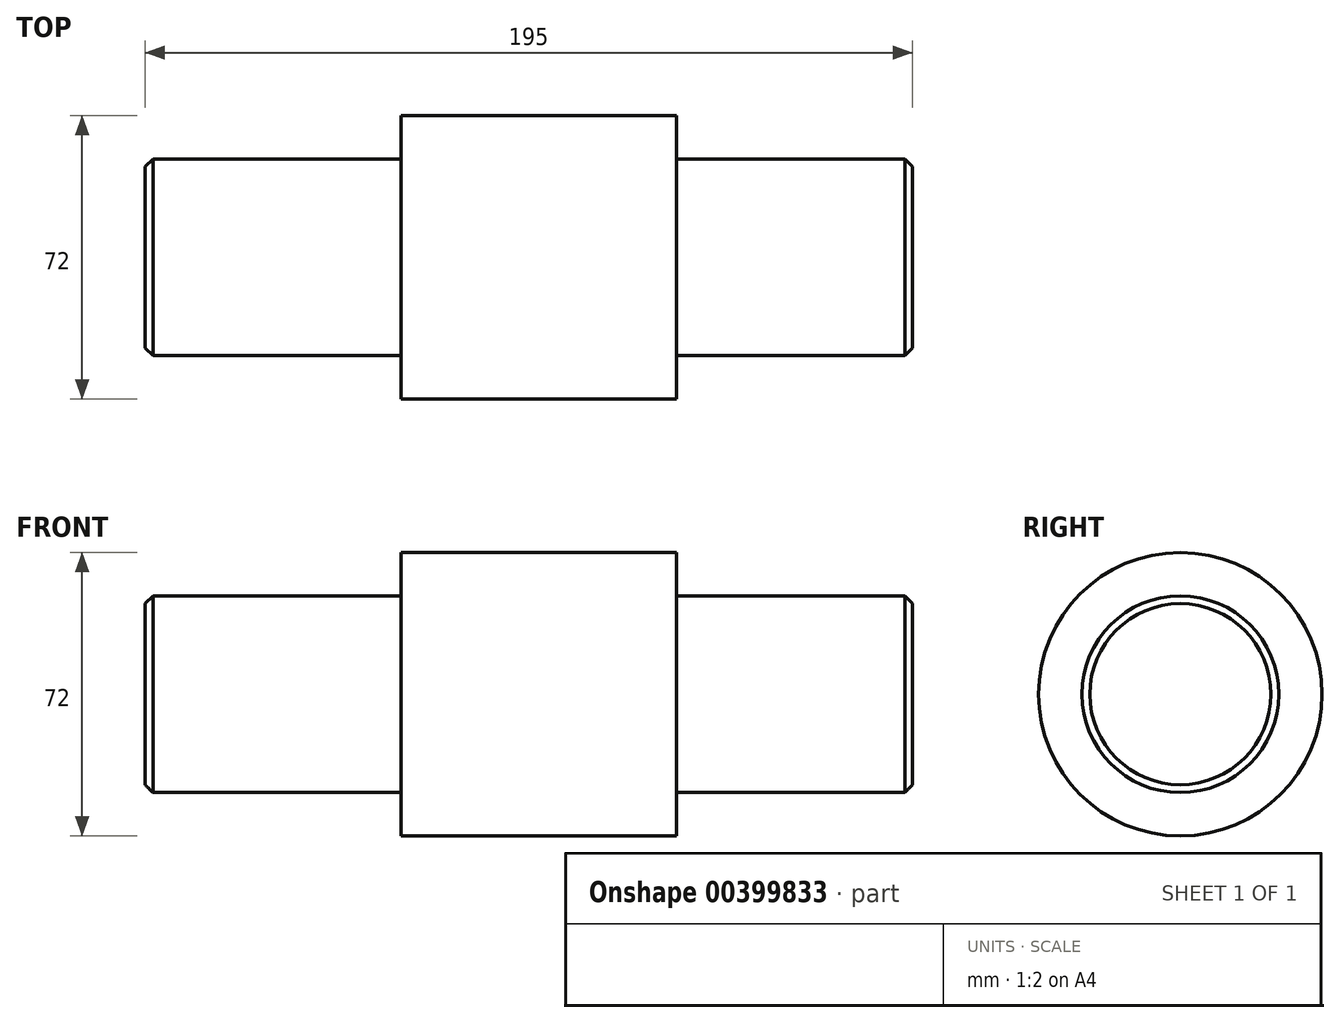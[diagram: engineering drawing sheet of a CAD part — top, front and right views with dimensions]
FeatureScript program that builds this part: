
annotation { "Feature Type Name" : "Feature", "Feature Type Description" : "" }
export const myFeature = defineFeature(function(context is Context, id is Id, definition is map)
    precondition{}
    {
        {
            var Q0;
            Q0=qCreatedBy(makeId("Right.planeOp"),FACE);
            var sketch = newSketch(context, id + "F0", { "sketchPlane" : qUnion([Q0])});
            skCircle(sketch, "E0", {"center": v(0, 0) * mm, "radius": 36 * mm});
            skSolve(sketch);
        }
        {
            var Q0;
            Q0=makeQuery(id+"F0.imprint","IMPRINT",FACE,{"disambiguationData":[TD([[makeQuery(id+"F0.imprint","IMPRINT",EDGE,{"derivedFrom":sQuery(id+"F0.wireOp",EDGE,"E0")}),1.0]])]});
            extrude(context, id + "F1", {"entities" : qUnion([Q0]), "depth" : (347.5 + 70) * mm, "hasSecondDirection" : true, "secondDirectionOppositeDirection" : true, "secondDirectionDepth" : -347.5 * mm});
        }
        {
            var Q0;
            Q0=qCreatedBy(makeId("Right.planeOp"),FACE);
            var sketch = newSketch(context, id + "F2", { "sketchPlane" : qUnion([Q0])});
            skCircle(sketch, "E1", {"center": v(0, 0) * mm, "radius": 25 * mm});
            skSolve(sketch);
        }
        {
            var Q0;
            Q0=makeQuery(id+"F2.imprint","IMPRINT",FACE,{"disambiguationData":[TD([[makeQuery(id+"F2.imprint","IMPRINT",EDGE,{"derivedFrom":sQuery(id+"F2.wireOp",EDGE,"E1")}),1.0]])]});
            extrude(context, id + "F3", {"entities" : qUnion([Q0]), "operationType" : NewBodyOperationType.ADD, "depth" : (347.5 + 130) * mm, "hasSecondDirection" : true, "secondDirectionOppositeDirection" : true, "secondDirectionDepth" : (-347.5 + 130 / 2) * mm});
        }
        {
            var Q0;
            Q0=makeQuery(id+"F3.opExtrude","CAP_EDGE",EDGE,{"disambiguationData":[OSD([sQuery(id+"F2.wireOp",EDGE,"E1")])],"isStart":false});
            var Q1;
            Q1=makeQuery(id+"F3.opExtrude","CAP_EDGE",EDGE,{"disambiguationData":[OSD([sQuery(id+"F2.wireOp",EDGE,"E1")])],"isStart":true});
            chamfer(context, id + "F4", {"entities" : qUnion([Q0, Q1]), "chamferType" : ChamferType.TWO_OFFSETS, "width1" : 2 * mm, "oppositeDirection" : false, "width2" : 2 * mm, "tangentPropagation" : true});
        }
    });
